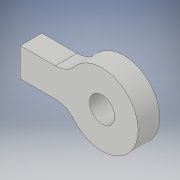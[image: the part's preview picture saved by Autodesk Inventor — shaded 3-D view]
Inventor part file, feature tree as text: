
AUTODESK INVENTOR PART (.ipt)
format: ipt  version: 2019 (Build 230136000, 136)  size: 111,104 bytes
history: native  units: mm
features: extrude x1, fillet x1, sketch x1
ambient origin geometry x8: Origin, YZ Plane, XZ Plane, XY Plane, X Axis, Y Axis, Z Axis, Center Point
bodies: Solid1 (feature_tree)
feature tree (3):
  extrude  "Extrusion1"  Depth=10.0mm
  fillet  "Fillet1"  Radius=7.0mm
  sketch  "Sketch1"  dims[d0=8.0mm d2=10.0mm d5=7.0mm d6=6.0mm d7=0.0mm d8=7.0mm d10=4.0mm d12=13.5mm]
